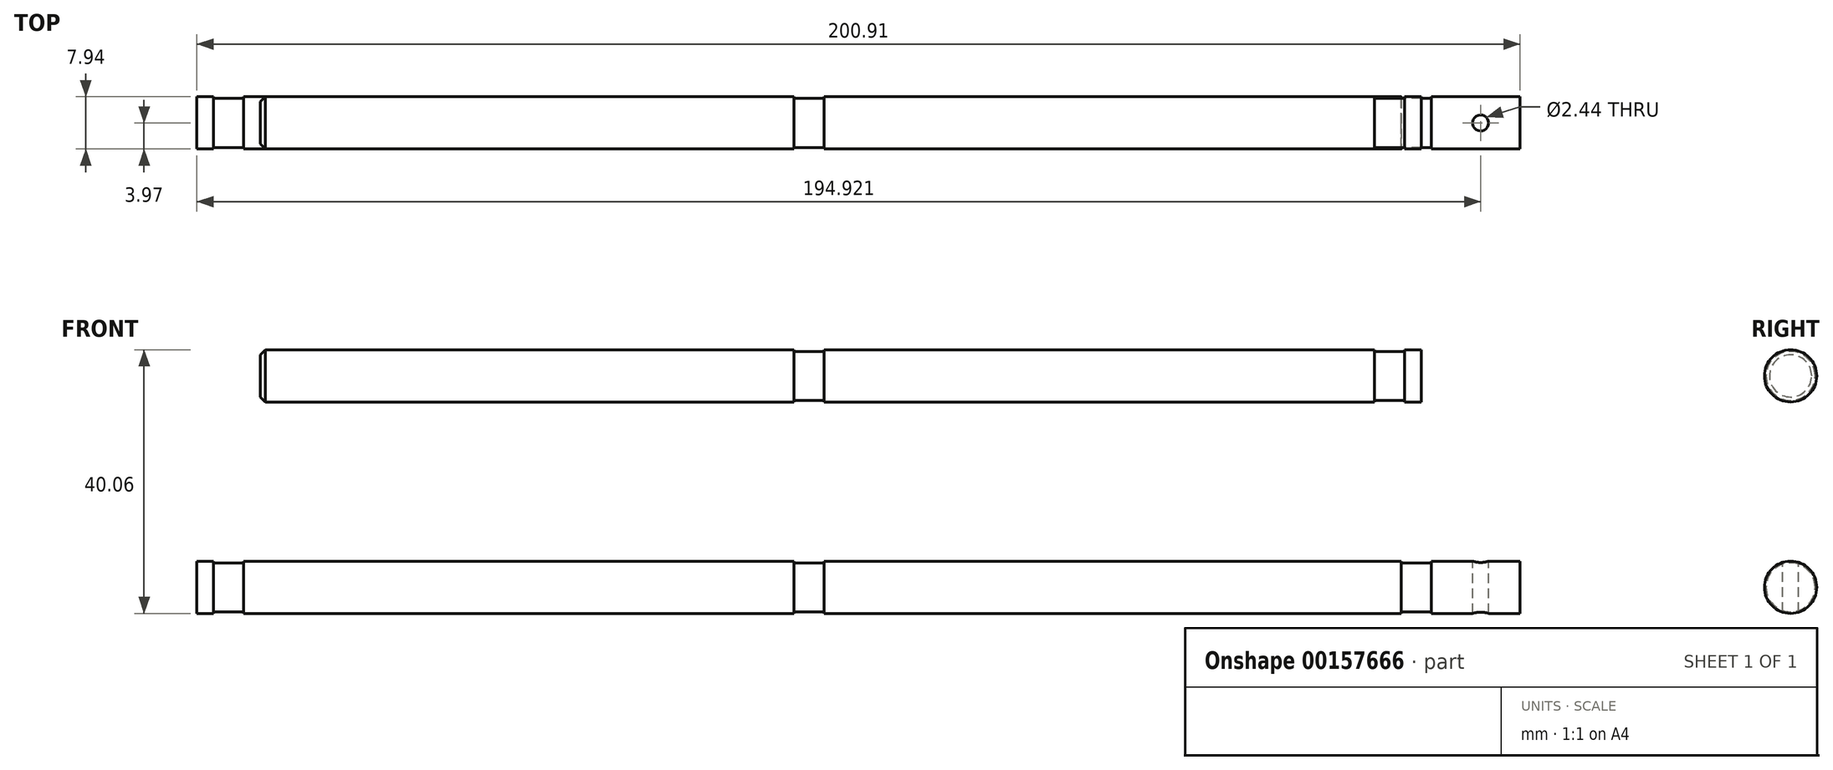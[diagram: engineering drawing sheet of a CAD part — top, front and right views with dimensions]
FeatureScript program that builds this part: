
annotation { "Feature Type Name" : "Feature", "Feature Type Description" : "" }
export const myFeature = defineFeature(function(context is Context, id is Id, definition is map)
    precondition{}
    {
        {
            var Q0;
            Q0=qCreatedBy(makeId("Right.planeOp"),FACE);
            var sketch = newSketch(context, id + "F0", { "sketchPlane" : qUnion([Q0])});
            skCircle(sketch, "E0", {"center": v(0, 0) * mm, "radius": 3.72 * mm});
            skSolve(sketch);
        }
        {
            var Q0;
            Q0=makeQuery(id+"F0.imprint","IMPRINT",FACE,{"disambiguationData":[TD([[makeQuery(id+"F0.imprint","IMPRINT",EDGE,{"derivedFrom":sQuery(id+"F0.wireOp",EDGE,"E0")}),1.0]])]});
            extrude(context, id + "F1", {"entities" : qUnion([Q0]), "depth" : 2.3 * mm, "hasSecondDirection" : true, "secondDirectionOppositeDirection" : true, "secondDirectionDepth" : 2.3 * mm});
        }
        {
            var Q0;
            Q0=makeQuery(id+"F1.opExtrude","CAP_FACE",FACE,{"disambiguationData":[OSD([sQuery(id+"F0.wireOp",EDGE,"E0")])],"isStart":false});
            var sketch = newSketch(context, id + "F2", { "sketchPlane" : qUnion([Q0])});
            skCircle(sketch, "E1", {"center": v(0, 0) * mm, "radius": 3.97 * mm});
            skSolve(sketch);
        }
        {
            var Q0;
            Q0=makeQuery(id+"F2.imprint","IMPRINT",FACE,{"disambiguationData":[TD([[makeQuery(id+"F2.imprint","IMPRINT",EDGE,{"derivedFrom":makeQuery(id+"F1.opExtrude","CAP_EDGE",EDGE,{"disambiguationData":[OSD([sQuery(id+"F0.wireOp",EDGE,"E0")])],"isStart":false})}),1.0]])]});
            var Q1;
            Q1=makeQuery(id+"F2.imprint","IMPRINT",FACE,{"disambiguationData":[TD([[makeQuery(id+"F2.imprint","IMPRINT",EDGE,{"derivedFrom":sQuery(id+"F2.wireOp",EDGE,"E1")}),1.0]])]});
            var Q2;
            Q2=sQuery(id+"F2.wireOp",EDGE,"E1");
            extrude(context, id + "F3", {"entities" : qUnion([Q0, Q1]), "operationType" : NewBodyOperationType.ADD, "surfaceEntities" : qUnion([Q2]), "depth" : 87.63 * mm});
        }
        {
            var Q0;
            Q0=makeQuery(id+"F3.opExtrude","CAP_FACE",FACE,{"disambiguationData":[OSD([sQuery(id+"F2.wireOp",EDGE,"E1")])],"isStart":false});
            var sketch = newSketch(context, id + "F4", { "sketchPlane" : qUnion([Q0])});
            skCircle(sketch, "E2", {"center": v(0, 0) * mm, "radius": 3.72 * mm});
            skSolve(sketch);
        }
        {
            var Q0;
            Q0=makeQuery(id+"F4.imprint","IMPRINT",FACE,{"disambiguationData":[TD([[makeQuery(id+"F4.imprint","IMPRINT",EDGE,{"derivedFrom":sQuery(id+"F4.wireOp",EDGE,"E2")}),1.0]])]});
            extrude(context, id + "F5", {"entities" : qUnion([Q0]), "operationType" : NewBodyOperationType.ADD, "depth" : 4.57 * mm});
        }
        {
            var Q0;
            Q0=makeQuery(id+"F5.opExtrude","CAP_FACE",FACE,{"disambiguationData":[OSD([sQuery(id+"F4.wireOp",EDGE,"E2")])],"isStart":false});
            var sketch = newSketch(context, id + "F6", { "sketchPlane" : qUnion([Q0])});
            skCircle(sketch, "E3", {"center": v(0, 0) * mm, "radius": 3.97 * mm});
            skSolve(sketch);
        }
        {
            var Q0;
            Q0=makeQuery(id+"F6.imprint","IMPRINT",FACE,{"disambiguationData":[TD([[makeQuery(id+"F6.imprint","IMPRINT",EDGE,{"derivedFrom":makeQuery(id+"F5.opExtrude","CAP_EDGE",EDGE,{"disambiguationData":[OSD([sQuery(id+"F4.wireOp",EDGE,"E2")])],"isStart":false})}),1.0]])]});
            var Q1;
            Q1=makeQuery(id+"F6.imprint","IMPRINT",FACE,{"disambiguationData":[TD([[makeQuery(id+"F6.imprint","IMPRINT",EDGE,{"derivedFrom":sQuery(id+"F6.wireOp",EDGE,"E3")}),1.0]])]});
            extrude(context, id + "F7", {"entities" : qUnion([Q0, Q1]), "operationType" : NewBodyOperationType.ADD, "depth" : 13.46 * mm});
        }
        {
            var Q0;
            Q0=makeQuery(id+"F1.opExtrude","CAP_FACE",FACE,{"disambiguationData":[OSD([sQuery(id+"F0.wireOp",EDGE,"E0")])],"isStart":true});
            var sketch = newSketch(context, id + "F8", { "sketchPlane" : qUnion([Q0])});
            skCircle(sketch, "E4", {"center": v(0, 0) * mm, "radius": 3.97 * mm});
            skSolve(sketch);
        }
        {
            var Q0;
            Q0=makeQuery(id+"F8.imprint","IMPRINT",FACE,{"disambiguationData":[TD([[makeQuery(id+"F8.imprint","IMPRINT",EDGE,{"derivedFrom":makeQuery(id+"F1.opExtrude","CAP_EDGE",EDGE,{"disambiguationData":[OSD([sQuery(id+"F0.wireOp",EDGE,"E0")])],"isStart":true})}),-1.0]])]});
            var Q1;
            Q1=makeQuery(id+"F8.imprint","IMPRINT",FACE,{"disambiguationData":[TD([[makeQuery(id+"F8.imprint","IMPRINT",EDGE,{"derivedFrom":sQuery(id+"F8.wireOp",EDGE,"E4")}),1.0]])]});
            extrude(context, id + "F9", {"entities" : qUnion([Q0, Q1]), "operationType" : NewBodyOperationType.ADD, "depth" : 83.57 * mm});
        }
        {
            var Q0;
            Q0=makeQuery(id+"F9.opExtrude","CAP_FACE",FACE,{"disambiguationData":[OSD([sQuery(id+"F8.wireOp",EDGE,"E4")])],"isStart":false});
            var sketch = newSketch(context, id + "F10", { "sketchPlane" : qUnion([Q0])});
            skCircle(sketch, "E5", {"center": v(0, 0) * mm, "radius": 3.72 * mm});
            skSolve(sketch);
        }
        {
            var Q0;
            Q0=makeQuery(id+"F10.imprint","IMPRINT",FACE,{"disambiguationData":[TD([[makeQuery(id+"F10.imprint","IMPRINT",EDGE,{"derivedFrom":sQuery(id+"F10.wireOp",EDGE,"E5")}),1.0]])]});
            extrude(context, id + "F11", {"entities" : qUnion([Q0]), "operationType" : NewBodyOperationType.ADD, "depth" : 4.57 * mm});
        }
        {
            var Q0;
            Q0=makeQuery(id+"F11.opExtrude","CAP_FACE",FACE,{"disambiguationData":[OSD([sQuery(id+"F10.wireOp",EDGE,"E5")])],"isStart":false});
            var sketch = newSketch(context, id + "F12", { "sketchPlane" : qUnion([Q0])});
            skCircle(sketch, "E6", {"center": v(0, 0) * mm, "radius": 3.97 * mm});
            skSolve(sketch);
        }
        {
            var Q0;
            Q0=makeQuery(id+"F12.imprint","IMPRINT",FACE,{"disambiguationData":[TD([[makeQuery(id+"F12.imprint","IMPRINT",EDGE,{"derivedFrom":makeQuery(id+"F11.opExtrude","CAP_EDGE",EDGE,{"disambiguationData":[OSD([sQuery(id+"F10.wireOp",EDGE,"E5")])],"isStart":false})}),1.0]])]});
            var Q1;
            Q1=makeQuery(id+"F12.imprint","IMPRINT",FACE,{"disambiguationData":[TD([[makeQuery(id+"F12.imprint","IMPRINT",EDGE,{"derivedFrom":sQuery(id+"F12.wireOp",EDGE,"E6")}),1.0]])]});
            extrude(context, id + "F13", {"entities" : qUnion([Q0, Q1]), "operationType" : NewBodyOperationType.ADD, "depth" : 2.54 * mm});
        }
        {
            var Q0;
            Q0=makeQuery(id+"F7.opExtrude","CAP_FACE",FACE,{"disambiguationData":[OSD([sQuery(id+"F6.wireOp",EDGE,"E3")])],"isStart":false});
            var sketch = newSketch(context, id + "F14", { "sketchPlane" : qUnion([Q0])});
            skLineSegment(sketch, "E7", {"start": v(0, 0) * mm, "end": v(0, 3.97) * mm, "construction": true});
            skSolve(sketch);
        }
        {
            var Q0;
            Q0=sQuery(id+"F14.wireOp",VERTEX,"E7.end");
            var Q1;
            Q1=qCreatedBy(makeId("Top.planeOp"),FACE);
            cPlane(context, id + "F15", {"entities" : qUnion([Q0, Q1]), "cplaneType" : CPlaneType.PLANE_POINT, "offset" : 25.4 * mm, "width" : 152.4 * mm, "height" : 152.4 * mm});
        }
        {
            var Q0;
            Q0=qCreatedBy(id+"F15.planeOp",FACE);
            var sketch = newSketch(context, id + "F16", { "sketchPlane" : qUnion([Q0])});
            skLineSegment(sketch, "E8", {"start": v(108.31, 0) * mm, "end": v(101.96, 0) * mm, "construction": true});
            skCircle(sketch, "E9", {"center": v(101.96, 0) * mm, "radius": 1.22 * mm});
            skSolve(sketch);
        }
        {
            var Q0;
            Q0=makeQuery(id+"F16.imprint","IMPRINT",FACE,{"disambiguationData":[TD([[makeQuery(id+"F16.imprint","IMPRINT",EDGE,{"derivedFrom":sQuery(id+"F16.wireOp",EDGE,"E9")}),1.0]])]});
            extrude(context, id + "F17", {"entities" : qUnion([Q0]), "operationType" : NewBodyOperationType.REMOVE, "oppositeDirection" : true, "depth" : 25.4 * mm});
        }
        {
            var Q0;
            Q0=qCreatedBy(makeId("Right.planeOp"),FACE);
            var sketch = newSketch(context, id + "F18", { "sketchPlane" : qUnion([Q0])});
            skCircle(sketch, "E10", {"center": v(0, 32.12) * mm, "radius": 3.72 * mm});
            skSolve(sketch);
        }
        {
            var Q0;
            Q0=makeQuery(id+"F18.imprint","IMPRINT",FACE,{"disambiguationData":[TD([[makeQuery(id+"F18.imprint","IMPRINT",EDGE,{"derivedFrom":sQuery(id+"F18.wireOp",EDGE,"E10")}),1.0]])]});
            var Q1;
            Q1=sQuery(id+"F18.wireOp",EDGE,"E10");
            extrude(context, id + "F19", {"entities" : qUnion([Q0]), "surfaceEntities" : qUnion([Q1]), "depth" : 2.3 * mm, "hasSecondDirection" : true, "secondDirectionOppositeDirection" : true, "secondDirectionDepth" : 2.3 * mm});
        }
        {
            var Q0;
            Q0=makeQuery(id+"F19.opExtrude","CAP_FACE",FACE,{"disambiguationData":[OSD([sQuery(id+"F18.wireOp",EDGE,"E10")])],"isStart":false});
            var sketch = newSketch(context, id + "F20", { "sketchPlane" : qUnion([Q0])});
            skCircle(sketch, "E11", {"center": v(0, 32.12) * mm, "radius": 3.97 * mm});
            skSolve(sketch);
        }
        {
            var Q0;
            Q0=makeQuery(id+"F20.imprint","IMPRINT",FACE,{"disambiguationData":[TD([[makeQuery(id+"F20.imprint","IMPRINT",EDGE,{"derivedFrom":makeQuery(id+"F19.opExtrude","CAP_EDGE",EDGE,{"disambiguationData":[OSD([sQuery(id+"F18.wireOp",EDGE,"E10")])],"isStart":false})}),1.0]])]});
            var Q1;
            Q1=makeQuery(id+"F20.imprint","IMPRINT",FACE,{"disambiguationData":[TD([[makeQuery(id+"F20.imprint","IMPRINT",EDGE,{"derivedFrom":sQuery(id+"F20.wireOp",EDGE,"E11")}),1.0]])]});
            extrude(context, id + "F21", {"entities" : qUnion([Q0, Q1]), "operationType" : NewBodyOperationType.ADD, "depth" : 83.57 * mm});
        }
        {
            var Q0;
            Q0=makeQuery(id+"F21.opExtrude","CAP_FACE",FACE,{"disambiguationData":[OSD([sQuery(id+"F20.wireOp",EDGE,"E11")])],"isStart":false});
            var sketch = newSketch(context, id + "F22", { "sketchPlane" : qUnion([Q0])});
            skCircle(sketch, "E12", {"center": v(0, 32.12) * mm, "radius": 3.72 * mm});
            skSolve(sketch);
        }
        {
            var Q0;
            Q0=makeQuery(id+"F22.imprint","IMPRINT",FACE,{"disambiguationData":[TD([[makeQuery(id+"F22.imprint","IMPRINT",EDGE,{"derivedFrom":sQuery(id+"F22.wireOp",EDGE,"E12")}),1.0]])]});
            extrude(context, id + "F23", {"entities" : qUnion([Q0]), "operationType" : NewBodyOperationType.ADD, "depth" : 4.57 * mm});
        }
        {
            var Q0;
            Q0=makeQuery(id+"F23.opExtrude","CAP_FACE",FACE,{"disambiguationData":[OSD([sQuery(id+"F22.wireOp",EDGE,"E12")])],"isStart":false});
            var sketch = newSketch(context, id + "F24", { "sketchPlane" : qUnion([Q0])});
            skCircle(sketch, "E13", {"center": v(0, 32.12) * mm, "radius": 3.97 * mm});
            skSolve(sketch);
        }
        {
            var Q0;
            Q0=makeQuery(id+"F24.imprint","IMPRINT",FACE,{"disambiguationData":[TD([[makeQuery(id+"F24.imprint","IMPRINT",EDGE,{"derivedFrom":makeQuery(id+"F23.opExtrude","CAP_EDGE",EDGE,{"disambiguationData":[OSD([sQuery(id+"F22.wireOp",EDGE,"E12")])],"isStart":false})}),1.0]])]});
            var Q1;
            Q1=makeQuery(id+"F24.imprint","IMPRINT",FACE,{"disambiguationData":[TD([[makeQuery(id+"F24.imprint","IMPRINT",EDGE,{"derivedFrom":sQuery(id+"F24.wireOp",EDGE,"E13")}),1.0]])]});
            extrude(context, id + "F25", {"entities" : qUnion([Q0, Q1]), "operationType" : NewBodyOperationType.ADD, "depth" : 2.54 * mm});
        }
        {
            var Q0;
            Q0=makeQuery(id+"F19.opExtrude","CAP_FACE",FACE,{"disambiguationData":[OSD([sQuery(id+"F18.wireOp",EDGE,"E10")])],"isStart":true});
            var sketch = newSketch(context, id + "F26", { "sketchPlane" : qUnion([Q0])});
            skCircle(sketch, "E14", {"center": v(0, 32.12) * mm, "radius": 3.97 * mm});
            skSolve(sketch);
        }
        {
            var Q0;
            Q0=makeQuery(id+"F26.imprint","IMPRINT",FACE,{"disambiguationData":[TD([[makeQuery(id+"F26.imprint","IMPRINT",EDGE,{"derivedFrom":makeQuery(id+"F19.opExtrude","CAP_EDGE",EDGE,{"disambiguationData":[OSD([sQuery(id+"F18.wireOp",EDGE,"E10")])],"isStart":true})}),-1.0]])]});
            var Q1;
            Q1=makeQuery(id+"F26.imprint","IMPRINT",FACE,{"disambiguationData":[TD([[makeQuery(id+"F26.imprint","IMPRINT",EDGE,{"derivedFrom":sQuery(id+"F26.wireOp",EDGE,"E14")}),1.0]])]});
            extrude(context, id + "F27", {"entities" : qUnion([Q0, Q1]), "operationType" : NewBodyOperationType.ADD, "depth" : 81.03 * mm});
        }
        {
            var Q0;
            Q0=makeQuery(id+"F27.opExtrude","CAP_EDGE",EDGE,{"disambiguationData":[OSD([sQuery(id+"F26.wireOp",EDGE,"E14")])],"isStart":false});
            chamfer(context, id + "F28", {"entities" : qUnion([Q0]), "width" : 0.76 * mm, "tangentPropagation" : true});
        }
    });
